# Revit family: IS_iLifeB_T4683_BIM_NL
name_source: partatom
category: Plumbing Fixtures
units: mm (PartAtom-declared; Revit-internal decimal feet)

## family parameters
Always vertical = No
Cut with Voids When Loaded = No
OmniClass Number = 23.45.05.21.11.11
OmniClass Title = Water Operated Water Closets
Part Type = Normal
Room Calculation Point = No
Round Connector Dimension = Use Diameter
Shared = No
Work Plane-Based = No

## types (3) — shared parameters
Accessories = https://www.idealstandard.nl
Afmetingen = 361 x 447 x 43 mm
AfstandsEenheid = Millimeter
AreaMeasurement = Internal
AreaUnits = millimetres
AssetType = Fixed
Auteur = Ideal Standard
BIMObjectName = IS_IdealStandard_WCseatsandcovers_i.lifeB_T4683
BIMobject category = Toilet Seats
BIMobject category code = toilet-seats
BIMobject main category = Sanitary
BIMobject main category code = sanitary
Beschrijvinggarantie = Herstellergarantie
BimObjectNaam = IS_IdealStandard_WCseatsandcovers_i.lifeB_T4683
Brand = Ideal Standard
Brand url = https://www.idealstandard.nl
Breedte = 361.039246
Category = Sanitary
Classification = Seats & Covers
ConnectionType = Plumbing
CurrencyUnit = €
CurrentRevision = 1
Date of publishing = 22/07/2022
Diepte = 447 mm
DurationUnit = Years
DuurEenheid = Jahre
Edition number = 1
ElementType = Fixed
ExpectedLife = 5
Features = wrapover seat, softclose,  easy-take off push button, adjustable hinge, in carton box, in master box, EU pallet
GarantieduurInstallatie = https://www.idealstandard.nl
Garantieonderdelen = https://www.idealstandard.nl
Garantieunits = Jahre
GemaaktOp = 22/07/2022
Help = https://www.idealstandard.nl
Hoogte = 42.5269979068979
Hulp = https://www.idealstandard.nl
IFC Classification = Sanitary Terminal
IfcExportAs = IfcSanitaryTerminalType
IfcExportType = WCSEAT
Installatieinstructies = https://www.idealstandard.nl
Installation instructions = https://www.idealstandard.nl
InstallationInstructions = https://www.idealstandard.nl
Lengte = 447 mm
LinearUnits = millimetres
MaintenanceInformation = https://www.idealstandard.nl
Manufacturer = Ideal Standard
Manufacturer name = Ideal Standard
ManufacturerURL = https://www.idealstandard.nl
Materiaal = Acryl-
Material = Fireclay
Material main = Fireclay
Merk = Ideal Standard
ModelReference = Ideal Standard i.life B wrapover seat, softclose,  easy-take off push button, adjustable hinge
NBS Reference Code = 45-35-70/391
NBS Reference Description = WC seats and covers
Name = WCseatsandcovers_i.lifeB_T4683_IdealStandard
NettWeight = 2.46
Nettogewicht = 2.46
NominalDepth = 447 mm
NominalHeight = 43 mm
NominalLength = 447 mm
NominalWidth = 361 mm
OmniClass Code = 23-31 19 00
OmniClass Description = Toilets
OppervlakteEenheid = Millimeter
PredefinedType = Seats & Cover
Product Guid = 5795b790-7cfa-440e-b28d-cecb00d0e279
Product SKU = T4683
Product certification = https://www.idealstandard.nl
Product data url = https://bimobject.com
Product family = I.Life B
Product group = Sanitary
Product name = I.Life b wrapover seat, softclose
Product url = https://www.idealstandard.nl
ProductInformation = https://www.idealstandard.nl
Productinformatie = https://www.idealstandard.nl
QR code = http://bimobject.com
Revisie = 1
SeatHasCover = No
SeatMaterial = Acrylic
SeatType = Soft Close
Shape = sculptured
Size = 361 x 447 x 43 mm
Space = Internal
SpareParts = https://www.idealstandard.nl
Technical description = https://www.idealstandard.nl
Telefoonnummer = 077 355 08 08
Toepassing = WC Seat & Cover
Typeconnectie = Installation
UNSPSC Code = 301815
URL = https://www.idealstandard.nl
Uniclass 2015 Code = Pr_40_20_93_95
Uniclass 2015 Name = WC seats and covers
Uniclass2015Beschrijving = WC seats and covers
Uniclass2015Code = Pr_40_20_93_95
Uniclass2015Referentie = Pr_40_20_93_95
Uniclass2015Title = WC seats and covers
Uniclass2015Version = v1.26
Urlproducent = https://www.idealstandard.nl
ValutaEenheid = Euro
Versie = 1
Version = 1
Verwachtelevensduur = 2
VolumeUnits = Liters
Volumeunits = Liter
Vorm = geformt
WRASURL = https://www.wrasapprovals.co.uk
WarrantyDescription = manufacturer warranty
WarrantyDurationUnit = Years
Weight Net (Kg) = 2.46
Wisselstukken = https://www.idealstandard.nl
Youtube clip = https://www.youtube.com
zero-valued in all types: BrutoGewicht, Cost, Default Elevation, Vervangingskosten

## per-type parameters (varying)
| type | Afwerking | Artikelnummer | Artikelomschrijving | Artikelreferentie | BarCode | Barcode | Color | Description | Eigenschappen | Finish | GTIN code | Kleur | MainColor | Model | ModelNumber | Referentie | SeatColor |
| T468301 - Ideal Standard i.life B wrapover seat, softclose,  easy-take off push button, adjustable hinge - White Finish | Weiss | T468301 | Ideal Standard i.life B Wickelsitz, Softclose, leicht abnehmbarer Druckknopf, verstellbares Scharnier, weiß, im Karton, im Umkarton, EU-Palette | T468301 | 8014140485971 | 8014140485971 | White | Ideal Standard i.life B wrapover seat, softclose,  easy-take off push button, adjustable hinge, white, in carton box, in master box, EU pallet | Wickelsitz, Softclose, leicht abnehmbarer Druckknopf, verstellbares Scharnier, weiß, im Karton, im Umkarton, EU-Palette | White | 8014140485971 | Weiss | White | T468301 | T468301 | Ideal Standard i.life B back-to-wall bowl, RimLS+, L-shape floor fixation in carton box | White |
| T4683HY - Ideal Standard i.life B wrapover seat, softclose,  easy-take off push button, adjustable hinge - White Antibacterial | Weiss Smartguard+ | T4683HY | Ideal Standard i.life B Wickelsitz, Softclose, leicht abnehmbarer Druckknopf, verstellbares Scharnier, weiß, im Karton, im Umkarton, EU-Palette | T4683HY | 8014140513384 | 8014140513384 | White Smartguard+ | Ideal Standard i.life B wrapover seat, softclose,  easy-take off push button, adjustable hinge, antibacterial , in carton box, in master box, EU pallet | Wickelsitz, Softclose, leicht abnehmbarer Druckknopf, verstellbares Scharnier, antibakteriell , im Karton, im Umkarton, EU-Palette | White Smartguard+ | 8014140513384 | Weiss Smartguard+ | White Smartguard+ | T4683HY | T4683HY | Ideal Standard i.life B wrapover seat, softclose,  easy-take off push button, adjustable hinge | White Smartguard+ |
| T468358 - Ideal Standard i.life B wrapover seat, softclose,  easy-take off push button, adjustable hinge - Glossy grey | Glänzend grau | T468358 | Ideal Standard i.life B Wickelsitz, Softclose, leicht abnehmbarer Druckknopf, verstellbares Scharnier, glänzend grau, im Karton, im Umkarton, EU-Palette | T468358 | 8014140511779 | 8014140511779 | Glossy grey | Ideal Standard i.life B wrapover seat, softclose,  easy-take off push button, adjustable hinge, glossy grey, in carton box, in master box, EU pallet | Wickelsitz, Softclose, leicht abnehmbarer Druckknopf, verstellbares Scharnier, antibakteriell , im Karton, im Umkarton, EU-Palette | Glossy grey | 8014140511779 | Glänzend grau | Glossy grey | T468358 | T468358 | Ideal Standard i.life B wrapover seat, softclose,  easy-take off push button, adjustable hinge | Glossy grey |

## geometry (parser evidence)
native form markers: Blend x4, Sweep x4
no freeform markers — native parametric forms only
